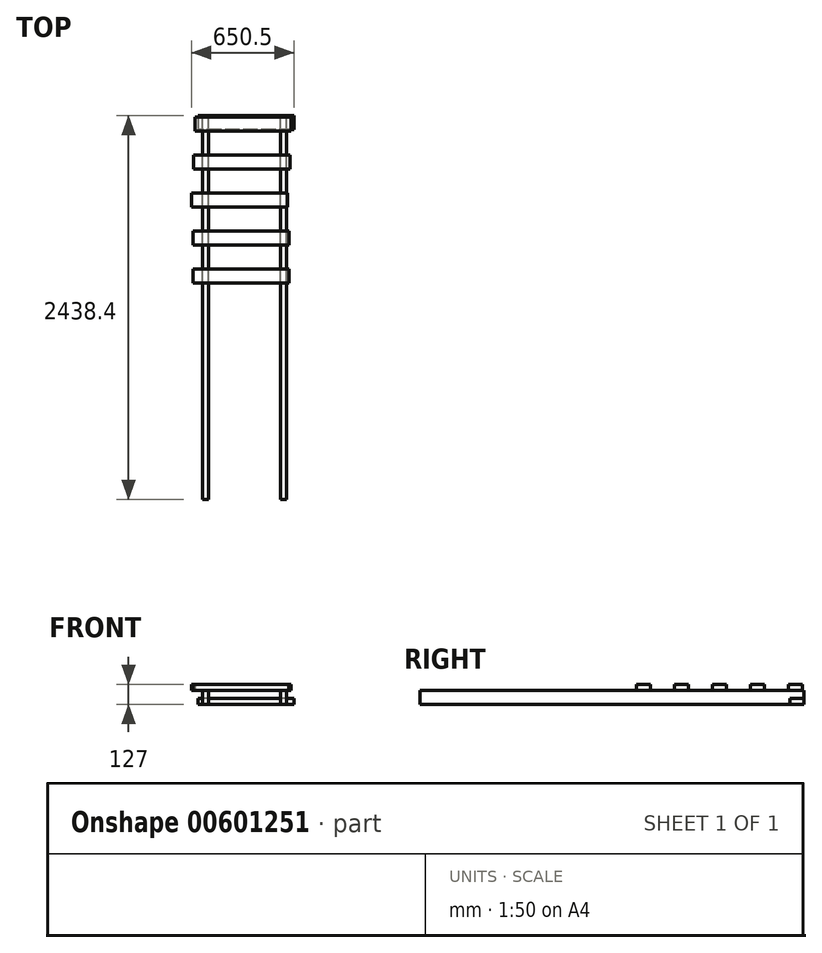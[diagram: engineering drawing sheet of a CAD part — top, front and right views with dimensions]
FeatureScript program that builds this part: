
annotation { "Feature Type Name" : "Feature", "Feature Type Description" : "" }
export const myFeature = defineFeature(function(context is Context, id is Id, definition is map)
    precondition{}
    {
        {
            var Q0;
            Q0=qCreatedBy(makeId("Front.planeOp"),FACE);
            var sketch = newSketch(context, id + "F0", { "sketchPlane" : qUnion([Q0])});
            skLineSegment(sketch, "E0.bottom", {"start": v(-457.2, 0) * mm, "end": v(-495.3, 0) * mm});
            skLineSegment(sketch, "E0.top", {"start": v(-457.2, 88.9) * mm, "end": v(-495.3, 88.9) * mm});
            skLineSegment(sketch, "E0.left", {"start": v(-457.2, 0) * mm, "end": v(-457.2, 88.9) * mm});
            skLineSegment(sketch, "E0.right", {"start": v(-495.3, 0) * mm, "end": v(-495.3, 88.9) * mm});
            skLineSegment(sketch, "E1.bottom", {"start": v(0, 0) * mm, "end": v(38.1, 0) * mm});
            skLineSegment(sketch, "E1.top", {"start": v(0, 88.9) * mm, "end": v(38.1, 88.9) * mm});
            skLineSegment(sketch, "E1.left", {"start": v(0, 0) * mm, "end": v(0, 88.9) * mm});
            skLineSegment(sketch, "E1.right", {"start": v(38.1, 0) * mm, "end": v(38.1, 88.9) * mm});
            skSolve(sketch);
        }
        {
            var Q0;
            Q0=makeQuery(id+"F0.imprint","IMPRINT",FACE,{"disambiguationData":[TD([[makeQuery(id+"F0.imprint","IMPRINT",EDGE,{"derivedFrom":sQuery(id+"F0.wireOp",EDGE,"E0.bottom")}),-1.0]])]});
            extrude(context, id + "F1", {"entities" : qUnion([Q0]), "depth" : 2438.4 * mm, "offsetDistance" : 25.4 * mm});
        }
        {
            var Q0;
            Q0=makeQuery(id+"F0.imprint","IMPRINT",FACE,{"disambiguationData":[TD([[makeQuery(id+"F0.imprint","IMPRINT",EDGE,{"derivedFrom":sQuery(id+"F0.wireOp",EDGE,"E1.bottom")}),1.0]])]});
            extrude(context, id + "F2", {"entities" : qUnion([Q0]), "depth" : 2438.4 * mm, "offsetDistance" : 25.4 * mm});
        }
        {
            var Q0;
            Q0=qCreatedBy(makeId("Top.planeOp"),FACE);
            var sketch = newSketch(context, id + "F3", { "sketchPlane" : qUnion([Q0])});
            skLineSegment(sketch, "E2.bottom", {"start": v(84.77, 0) * mm, "end": v(-524.83, 0) * mm});
            skLineSegment(sketch, "E2.top", {"start": v(84.77, -88.9) * mm, "end": v(-524.83, -88.9) * mm});
            skLineSegment(sketch, "E2.left", {"start": v(84.77, 0) * mm, "end": v(84.77, -88.9) * mm});
            skLineSegment(sketch, "E2.right", {"start": v(-524.83, 0) * mm, "end": v(-524.83, -88.9) * mm});
            skSolve(sketch);
        }
        {
            var Q0;
            Q0=makeQuery(id+"F3.imprint","IMPRINT",FACE,{"disambiguationData":[TD([[makeQuery(id+"F3.imprint","IMPRINT",EDGE,{"derivedFrom":sQuery(id+"F3.wireOp",EDGE,"E2.bottom")}),1.0]])]});
            extrude(context, id + "F4", {"entities" : qUnion([Q0]), "depth" : 38.1 * mm, "offsetDistance" : 25.4 * mm});
        }
        {
            var Q0;
            Q0=makeQuery(id+"F4.opExtrude","CAP_FACE",FACE,{"disambiguationData":[OSD([sQuery(id+"F3.wireOp",EDGE,"E2.bottom"),sQuery(id+"F3.wireOp",EDGE,"E2.top"),sQuery(id+"F3.wireOp",EDGE,"E2.left"),sQuery(id+"F3.wireOp",EDGE,"E2.right")])],"isStart":false});
            cPlane(context, id + "F5", {"entities" : qUnion([Q0]), "cplaneType" : CPlaneType.OFFSET, "offset" : 50.8 * mm, "width" : 152.4 * mm, "height" : 152.4 * mm});
        }
        {
            var Q0;
            Q0=qCreatedBy(id+"F5.planeOp",FACE);
            var sketch = newSketch(context, id + "F6", { "sketchPlane" : qUnion([Q0])});
            skLineSegment(sketch, "E3.bottom", {"start": v(-544.25, -9.68) * mm, "end": v(65.35, -9.68) * mm});
            skLineSegment(sketch, "E3.top", {"start": v(-544.25, -98.58) * mm, "end": v(65.35, -98.58) * mm});
            skLineSegment(sketch, "E3.left", {"start": v(-544.25, -9.68) * mm, "end": v(-544.25, -98.58) * mm});
            skLineSegment(sketch, "E3.right", {"start": v(65.35, -9.68) * mm, "end": v(65.35, -98.58) * mm});
            skLineSegment(sketch, "E4.bottom", {"start": v(-551.55, -250.98) * mm, "end": v(58.05, -250.98) * mm});
            skLineSegment(sketch, "E4.top", {"start": v(-551.55, -339.88) * mm, "end": v(58.05, -339.88) * mm});
            skLineSegment(sketch, "E4.left", {"start": v(-551.55, -250.98) * mm, "end": v(-551.55, -339.88) * mm});
            skLineSegment(sketch, "E4.right", {"start": v(58.05, -250.98) * mm, "end": v(58.05, -339.88) * mm});
            skLineSegment(sketch, "E5.bottom", {"start": v(-565.73, -492.28) * mm, "end": v(43.87, -492.28) * mm});
            skLineSegment(sketch, "E5.top", {"start": v(-565.73, -581.18) * mm, "end": v(43.87, -581.18) * mm});
            skLineSegment(sketch, "E5.left", {"start": v(-565.73, -492.28) * mm, "end": v(-565.73, -581.18) * mm});
            skLineSegment(sketch, "E5.right", {"start": v(43.87, -492.28) * mm, "end": v(43.87, -581.18) * mm});
            skLineSegment(sketch, "E6.bottom", {"start": v(-557.6, -733.58) * mm, "end": v(52, -733.58) * mm});
            skLineSegment(sketch, "E6.top", {"start": v(-557.6, -822.48) * mm, "end": v(52, -822.48) * mm});
            skLineSegment(sketch, "E6.left", {"start": v(-557.6, -733.58) * mm, "end": v(-557.6, -822.48) * mm});
            skLineSegment(sketch, "E6.right", {"start": v(52, -733.58) * mm, "end": v(52, -822.48) * mm});
            skLineSegment(sketch, "E7.bottom", {"start": v(-557.6, -974.88) * mm, "end": v(52, -974.88) * mm});
            skLineSegment(sketch, "E7.top", {"start": v(-557.6, -1063.78) * mm, "end": v(52, -1063.78) * mm});
            skLineSegment(sketch, "E7.left", {"start": v(-557.6, -974.88) * mm, "end": v(-557.6, -1063.78) * mm});
            skLineSegment(sketch, "E7.right", {"start": v(52, -974.88) * mm, "end": v(52, -1063.78) * mm});
            skSolve(sketch);
        }
        {
            var Q0;
            Q0=makeQuery(id+"F6.imprint","IMPRINT",FACE,{"disambiguationData":[TD([[makeQuery(id+"F6.imprint","IMPRINT",EDGE,{"derivedFrom":sQuery(id+"F6.wireOp",EDGE,"E3.bottom")}),-1.0]])]});
            extrude(context, id + "F7", {"entities" : qUnion([Q0]), "depth" : 38.1 * mm, "offsetDistance" : 25.4 * mm});
        }
        {
            var Q0;
            Q0 = qSketchRegion(id + "F6", true);
            extrude(context, id + "F8", {"entities" : qUnion([Q0]), "depth" : 38.1 * mm, "offsetDistance" : 25.4 * mm});
        }
    });
